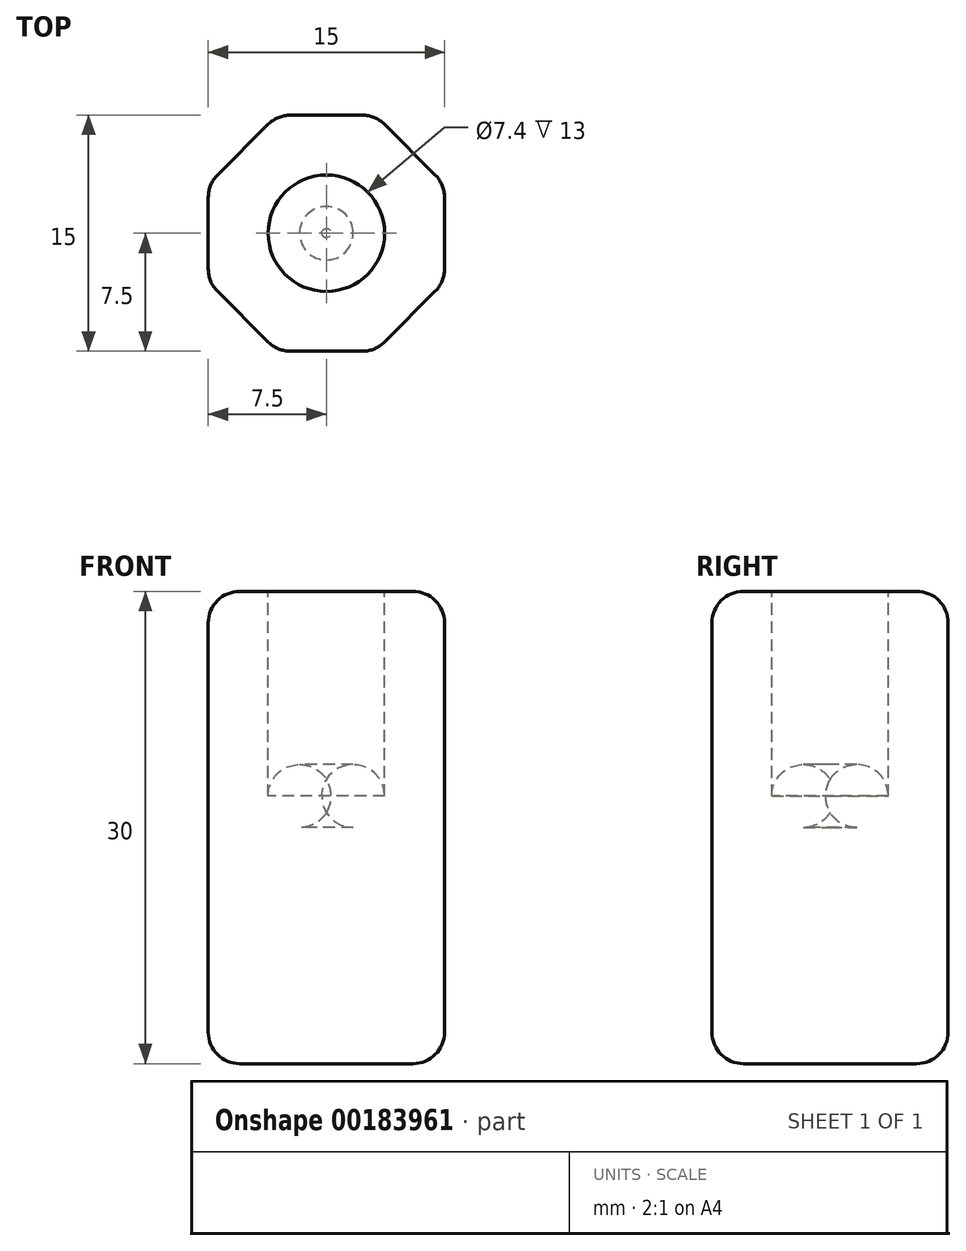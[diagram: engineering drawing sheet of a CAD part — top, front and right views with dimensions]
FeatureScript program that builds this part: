
annotation { "Feature Type Name" : "Feature", "Feature Type Description" : "" }
export const myFeature = defineFeature(function(context is Context, id is Id, definition is map)
    precondition{}
    {
        {
            var Q0;
            Q0=qCreatedBy(makeId("Top.planeOp"),FACE);
            var sketch = newSketch(context, id + "F0", { "sketchPlane" : qUnion([Q0])});
            skCircle(sketch, "E0.cCircle", {"center": v(0, 0) * mm, "radius": 7.5 * mm, "construction": true});
            skLineSegment(sketch, "E0.0", {"start": v(-7.5, -3.1) * mm, "end": v(-7.5, 3.1) * mm});
            skLineSegment(sketch, "E0.1", {"start": v(-7.5, 3.1) * mm, "end": v(-3.1, 7.5) * mm});
            skLineSegment(sketch, "E0.2", {"start": v(-3.1, 7.5) * mm, "end": v(3.1, 7.5) * mm});
            skLineSegment(sketch, "E0.3", {"start": v(3.1, 7.5) * mm, "end": v(7.5, 3.1) * mm});
            skLineSegment(sketch, "E0.4", {"start": v(7.5, 3.1) * mm, "end": v(7.5, -3.1) * mm});
            skLineSegment(sketch, "E0.5", {"start": v(7.5, -3.1) * mm, "end": v(3.1, -7.5) * mm});
            skLineSegment(sketch, "E0.6", {"start": v(3.1, -7.5) * mm, "end": v(-3.1, -7.5) * mm});
            skLineSegment(sketch, "E0.7", {"start": v(-3.1, -7.5) * mm, "end": v(-7.5, -3.1) * mm});
            skPoint(sketch, "E0.0.midPoint", {"position": v(-7.5, 0) * mm});
            skSolve(sketch);
        }
        {
            var Q0;
            Q0 = qSketchRegion(id + "F0", true);
            extrude(context, id + "F1", {"entities" : qUnion([Q0]), "depth" : 30 * mm});
        }
        {
            var Q0;
            Q0=makeQuery(id+"F1.opExtrude","CAP_FACE",FACE,{"disambiguationData":[OSD([sQuery(id+"F0.wireOp",EDGE,"E0.0"),sQuery(id+"F0.wireOp",EDGE,"E0.1"),sQuery(id+"F0.wireOp",EDGE,"E0.2"),sQuery(id+"F0.wireOp",EDGE,"E0.3"),sQuery(id+"F0.wireOp",EDGE,"E0.4"),sQuery(id+"F0.wireOp",EDGE,"E0.5"),sQuery(id+"F0.wireOp",EDGE,"E0.6"),sQuery(id+"F0.wireOp",EDGE,"E0.7")])],"isStart":false});
            var sketch = newSketch(context, id + "F2", { "sketchPlane" : qUnion([Q0])});
            skCircle(sketch, "E1", {"center": v(0, 0) * mm, "radius": 3.7 * mm});
            skSolve(sketch);
        }
        {
            var Q0;
            Q0 = qSketchRegion(id + "F2", true);
            extrude(context, id + "F3", {"entities" : qUnion([Q0]), "operationType" : NewBodyOperationType.REMOVE, "oppositeDirection" : true, "depth" : 15 * mm});
        }
        {
            var Q0;
            Q0=makeQuery(id+"F1.opExtrude","CAP_EDGE",EDGE,{"disambiguationData":[OSD([sQuery(id+"F0.wireOp",EDGE,"E0.5")])],"isStart":true});
            var Q1;
            Q1=makeQuery(id+"F1.opExtrude","SWEPT_EDGE",EDGE,{"disambiguationData":[OSD([sQuery(id+"F0.wireOp",EDGE,"E0.4"),sQuery(id+"F0.wireOp",EDGE,"E0.5")])]});
            var Q2;
            Q2=makeQuery(id+"F1.opExtrude","SWEPT_EDGE",EDGE,{"disambiguationData":[OSD([sQuery(id+"F0.wireOp",EDGE,"E0.3"),sQuery(id+"F0.wireOp",EDGE,"E0.4")])]});
            var Q3;
            Q3=makeQuery(id+"F1.opExtrude","CAP_EDGE",EDGE,{"disambiguationData":[OSD([sQuery(id+"F0.wireOp",EDGE,"E0.6")])],"isStart":true});
            var Q4;
            Q4=makeQuery(id+"F1.opExtrude","CAP_EDGE",EDGE,{"disambiguationData":[OSD([sQuery(id+"F0.wireOp",EDGE,"E0.2")])],"isStart":true});
            var Q5;
            Q5=makeQuery(id+"F1.opExtrude","CAP_EDGE",EDGE,{"disambiguationData":[OSD([sQuery(id+"F0.wireOp",EDGE,"E0.4")])],"isStart":false});
            var Q6;
            Q6=makeQuery(id+"F1.opExtrude","CAP_EDGE",EDGE,{"disambiguationData":[OSD([sQuery(id+"F0.wireOp",EDGE,"E0.3")])],"isStart":true});
            var Q7;
            Q7=makeQuery(id+"F1.opExtrude","CAP_EDGE",EDGE,{"disambiguationData":[OSD([sQuery(id+"F0.wireOp",EDGE,"E0.7")])],"isStart":true});
            var Q8;
            Q8=makeQuery(id+"F1.opExtrude","CAP_EDGE",EDGE,{"disambiguationData":[OSD([sQuery(id+"F0.wireOp",EDGE,"E0.4")])],"isStart":true});
            var Q9;
            Q9=makeQuery(id+"F1.opExtrude","CAP_EDGE",EDGE,{"disambiguationData":[OSD([sQuery(id+"F0.wireOp",EDGE,"E0.0")])],"isStart":true});
            var Q10;
            Q10=makeQuery(id+"F1.opExtrude","SWEPT_EDGE",EDGE,{"disambiguationData":[OSD([sQuery(id+"F0.wireOp",EDGE,"E0.0"),sQuery(id+"F0.wireOp",EDGE,"E0.1")])]});
            var Q11;
            Q11=makeQuery(id+"F1.opExtrude","SWEPT_EDGE",EDGE,{"disambiguationData":[OSD([sQuery(id+"F0.wireOp",EDGE,"E0.1"),sQuery(id+"F0.wireOp",EDGE,"E0.2")])]});
            var Q12;
            Q12=makeQuery(id+"F1.opExtrude","SWEPT_EDGE",EDGE,{"disambiguationData":[OSD([sQuery(id+"F0.wireOp",EDGE,"E0.6"),sQuery(id+"F0.wireOp",EDGE,"E0.7")])]});
            var Q13;
            Q13=makeQuery(id+"F1.opExtrude","CAP_EDGE",EDGE,{"disambiguationData":[OSD([sQuery(id+"F0.wireOp",EDGE,"E0.1")])],"isStart":false});
            var Q14;
            Q14=makeQuery(id+"F1.opExtrude","SWEPT_EDGE",EDGE,{"disambiguationData":[OSD([sQuery(id+"F0.wireOp",EDGE,"E0.0"),sQuery(id+"F0.wireOp",EDGE,"E0.7")])]});
            var Q15;
            Q15=makeQuery(id+"F1.opExtrude","CAP_EDGE",EDGE,{"disambiguationData":[OSD([sQuery(id+"F0.wireOp",EDGE,"E0.7")])],"isStart":false});
            var Q16;
            Q16=makeQuery(id+"F1.opExtrude","CAP_EDGE",EDGE,{"disambiguationData":[OSD([sQuery(id+"F0.wireOp",EDGE,"E0.1")])],"isStart":true});
            var Q17;
            Q17=makeQuery(id+"F1.opExtrude","SWEPT_EDGE",EDGE,{"disambiguationData":[OSD([sQuery(id+"F0.wireOp",EDGE,"E0.5"),sQuery(id+"F0.wireOp",EDGE,"E0.6")])]});
            var Q18;
            Q18=makeQuery(id+"F1.opExtrude","CAP_EDGE",EDGE,{"disambiguationData":[OSD([sQuery(id+"F0.wireOp",EDGE,"E0.5")])],"isStart":false});
            var Q19;
            Q19=makeQuery(id+"F3.boolean.opBoolean","COPY",EDGE,{"derivedFrom":makeQuery(id+"F3.opExtrude","CAP_EDGE",EDGE,{"disambiguationData":[OSD([sQuery(id+"F2.wireOp",EDGE,"E1")])],"isStart":false})});
            var Q20;
            Q20=makeQuery(id+"F1.opExtrude","CAP_EDGE",EDGE,{"disambiguationData":[OSD([sQuery(id+"F0.wireOp",EDGE,"E0.6")])],"isStart":false});
            var Q21;
            Q21=makeQuery(id+"F1.opExtrude","CAP_EDGE",EDGE,{"disambiguationData":[OSD([sQuery(id+"F0.wireOp",EDGE,"E0.2")])],"isStart":false});
            var Q22;
            Q22=makeQuery(id+"F1.opExtrude","SWEPT_EDGE",EDGE,{"disambiguationData":[OSD([sQuery(id+"F0.wireOp",EDGE,"E0.2"),sQuery(id+"F0.wireOp",EDGE,"E0.3")])]});
            var Q23;
            Q23=makeQuery(id+"F3.boolean.opBoolean","COPY",EDGE,{"derivedFrom":makeQuery(id+"F3.opExtrude","CAP_EDGE",EDGE,{"disambiguationData":[OSD([sQuery(id+"F2.wireOp",EDGE,"E1")])],"isStart":true})});
            var Q24;
            Q24=makeQuery(id+"F1.opExtrude","CAP_EDGE",EDGE,{"disambiguationData":[OSD([sQuery(id+"F0.wireOp",EDGE,"E0.3")])],"isStart":false});
            var Q25;
            Q25=makeQuery(id+"F1.opExtrude","CAP_EDGE",EDGE,{"disambiguationData":[OSD([sQuery(id+"F0.wireOp",EDGE,"E0.0")])],"isStart":false});
            fillet(context, id + "F4", {"entities" : qUnion([Q0, Q1, Q2, Q3, Q4, Q5, Q6, Q7, Q8, Q9, Q10, Q11, Q12, Q13, Q14, Q15, Q16, Q17, Q18, Q19, Q20, Q21, Q22, Q23, Q24, Q25]), "radius" : 2 * mm, "tangentPropagation" : true, "allowEdgeOverflow" : false});
        }
    });
